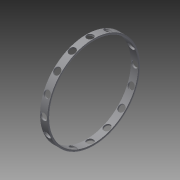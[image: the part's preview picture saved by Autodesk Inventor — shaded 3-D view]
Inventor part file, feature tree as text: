
AUTODESK INVENTOR PART (.ipt)
format: ipt  version: 2014 SP2 (Build 180246200, 246)  size: 229,376 bytes
history: native  units: mm
features: other x119, revolve x2, sketch x2, pattern_circular x1
ambient origin geometry x8: Origin, YZ Plane, XZ Plane, XY Plane, X Axis, Y Axis, Z Axis, Center Point
bodies: Solid1 (feature_tree)
feature tree (124):
  revolve  "Revolution1"  Angle=360.0deg
  revolve  "Revolution2"  [1 undecoded]
  pattern_circular  "Circular Pattern1"  [2 undecoded]
  other  "1_XY"
  other  "1_YZ"
  other  "1_ZX"
  other  "1_X"
  other  "1_Y"
  other  "1_Z"
  other  "1_Center"
  other  "2_1_XY"
  other  "2_1_YZ"
  other  "2_1_ZX"
  other  "2_1_X"
  other  "2_1_Y"
  other  "2_1_Z"
  other  "2_1_Center"
  other  "2_10_XY"
  other  "2_10_YZ"
  other  "2_10_ZX"
  other  "2_10_X"
  other  "2_10_Y"
  other  "2_10_Z"
  other  "2_10_Center"
  other  "2_11_XY"
  other  "2_11_YZ"
  other  "2_11_ZX"
  other  "2_11_X"
  other  "2_11_Y"
  other  "2_11_Z"
  other  "2_11_Center"
  other  "2_12_XY"
  other  "2_12_YZ"
  other  "2_12_ZX"
  other  "2_12_X"
  other  "2_12_Y"
  other  "2_12_Z"
  other  "2_12_Center"
  other  "2_13_XY"
  other  "2_13_YZ"
  other  "2_13_ZX"
  other  "2_13_X"
  other  "2_13_Y"
  other  "2_13_Z"
  other  "2_13_Center"
  other  "2_14_XY"
  other  "2_14_YZ"
  other  "2_14_ZX"
  other  "2_14_X"
  other  "2_14_Y"
  other  "2_14_Z"
  other  "2_14_Center"
  other  "2_15_XY"
  other  "2_15_YZ"
  other  "2_15_ZX"
  other  "2_15_X"
  other  "2_15_Y"
  other  "2_15_Z"
  other  "2_15_Center"
  other  "2_16_XY"
  other  "2_16_YZ"
  other  "2_16_ZX"
  other  "2_16_X"
  other  "2_16_Y"
  other  "2_16_Z"
  other  "2_16_Center"
  other  "2_2_XY"
  other  "2_2_YZ"
  other  "2_2_ZX"
  other  "2_2_X"
  other  "2_2_Y"
  other  "2_2_Z"
  other  "2_2_Center"
  other  "2_3_XY"
  other  "2_3_YZ"
  other  "2_3_ZX"
  other  "2_3_X"
  other  "2_3_Y"
  other  "2_3_Z"
  other  "2_3_Center"
  other  "2_4_XY"
  other  "2_4_YZ"
  other  "2_4_ZX"
  other  "2_4_X"
  other  "2_4_Y"
  other  "2_4_Z"
  other  "2_4_Center"
  other  "2_5_XY"
  other  "2_5_YZ"
  other  "2_5_ZX"
  other  "2_5_X"
  other  "2_5_Y"
  other  "2_5_Z"
  other  "2_5_Center"
  other  "2_6_XY"
  other  "2_6_YZ"
  other  "2_6_ZX"
  other  "2_6_X"
  other  "2_6_Y"
  other  "2_6_Z"
  other  "2_6_Center"
  other  "2_7_XY"
  other  "2_7_YZ"
  other  "2_7_ZX"
  other  "2_7_X"
  other  "2_7_Y"
  other  "2_7_Z"
  other  "2_7_Center"
  other  "2_8_XY"
  other  "2_8_YZ"
  other  "2_8_ZX"
  other  "2_8_X"
  other  "2_8_Y"
  other  "2_8_Z"
  other  "2_8_Center"
  other  "2_9_XY"
  other  "2_9_YZ"
  other  "2_9_ZX"
  other  "2_9_X"
  other  "2_9_Y"
  other  "2_9_Z"
  other  "2_9_Center"
  sketch  "Sketch_6"  dims[d2=160.0mm d3=22.5deg]
  sketch  "Sketch_2"  dims[d0=360.0deg d1=360.0deg]
note: 3 required parameter values undecoded (feature->parameter linkage not recoverable at this tier; creation-order binding heuristic only, values carry confidence <= 0.55)
